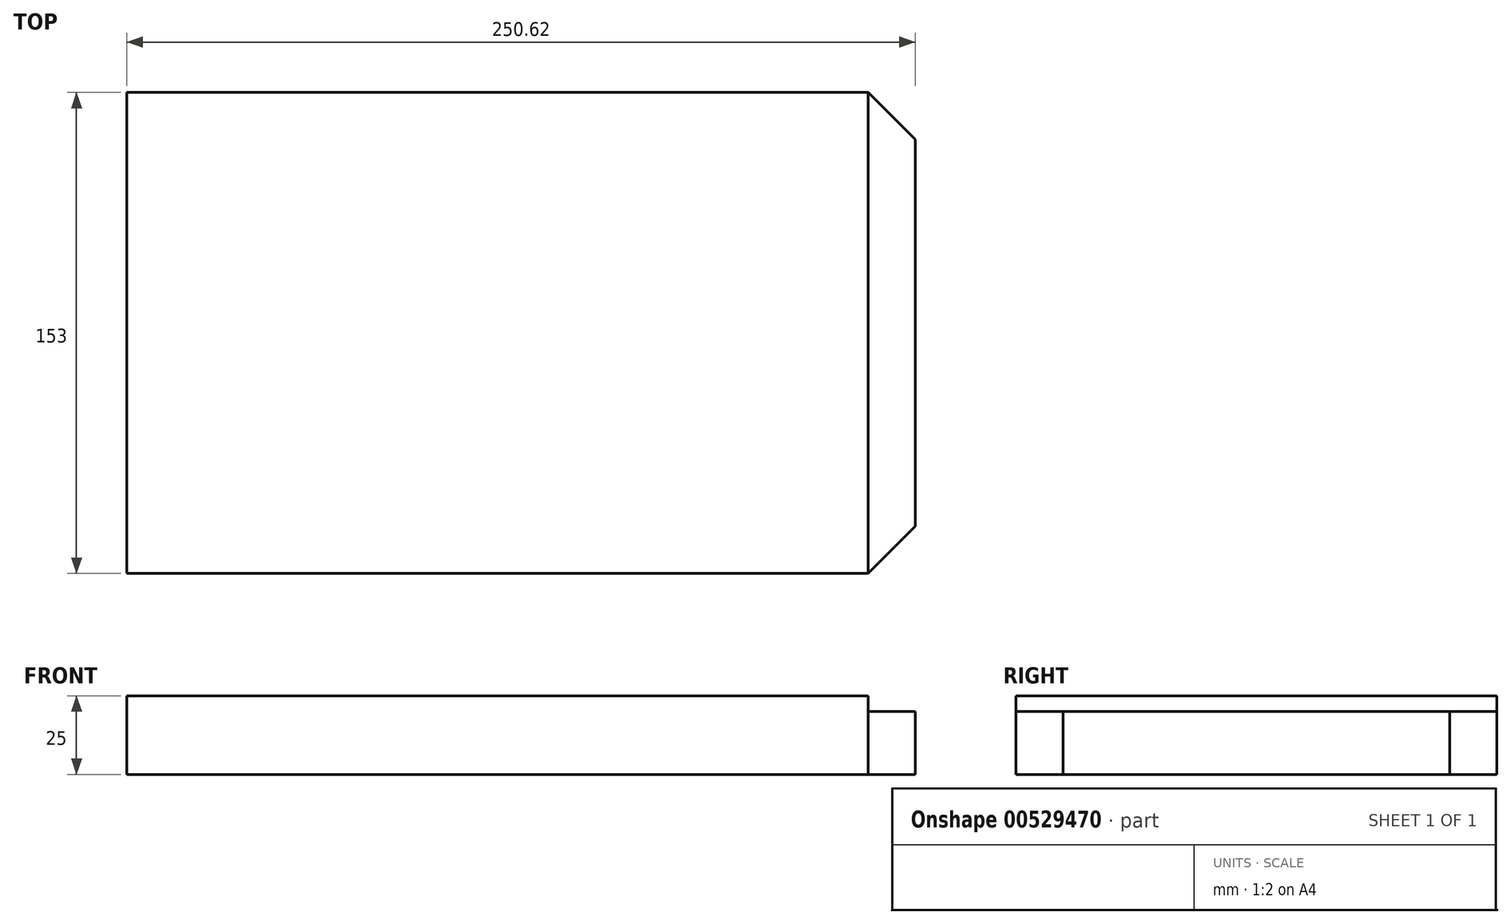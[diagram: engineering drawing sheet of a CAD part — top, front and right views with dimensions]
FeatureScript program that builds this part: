
annotation { "Feature Type Name" : "Feature", "Feature Type Description" : "" }
export const myFeature = defineFeature(function(context is Context, id is Id, definition is map)
    precondition{}
    {
        {
            var Q0;
            Q0=qCreatedBy(makeId("Top.planeOp"),FACE);
            var sketch = newSketch(context, id + "F0", { "sketchPlane" : qUnion([Q0])});
            skLineSegment(sketch, "E0.bottom", {"start": v(117.81, 76.5) * mm, "end": v(-117.81, 76.5) * mm});
            skLineSegment(sketch, "E0.top", {"start": v(117.81, -76.5) * mm, "end": v(-117.81, -76.5) * mm});
            skLineSegment(sketch, "E0.left", {"start": v(117.81, 76.5) * mm, "end": v(117.81, -76.5) * mm});
            skLineSegment(sketch, "E0.right", {"start": v(-117.81, 76.5) * mm, "end": v(-117.81, -76.5) * mm});
            skPoint(sketch, "E0.middle", {"position": v(0, 0) * mm});
            skLineSegment(sketch, "E1", {"start": v(117.81, 76.5) * mm, "end": v(132.8, 61.5) * mm});
            skLineSegment(sketch, "E2", {"start": v(132.8, 61.5) * mm, "end": v(132.8, -61.5) * mm});
            skLineSegment(sketch, "E3", {"start": v(132.8, -61.5) * mm, "end": v(117.81, -76.5) * mm});
            skSolve(sketch);
        }
        {
            var Q0;
            Q0=makeQuery(id+"F0.imprint","IMPRINT",FACE,{"disambiguationData":[TD([[makeQuery(id+"F0.imprint","IMPRINT",EDGE,{"derivedFrom":sQuery(id+"F0.wireOp",EDGE,"E0.bottom")}),1.0]])]});
            extrude(context, id + "F1", {"entities" : qUnion([Q0]), "depth" : 25 * mm, "offsetDistance" : 25 * mm});
        }
        {
            var Q0;
            Q0=makeQuery(id+"F0.imprint","IMPRINT",FACE,{"disambiguationData":[TD([[makeQuery(id+"F0.imprint","IMPRINT",EDGE,{"derivedFrom":sQuery(id+"F0.wireOp",EDGE,"E0.left")}),1.0]])]});
            extrude(context, id + "F2", {"entities" : qUnion([Q0]), "operationType" : NewBodyOperationType.ADD, "depth" : 20 * mm, "offsetDistance" : 25 * mm});
        }
    });
